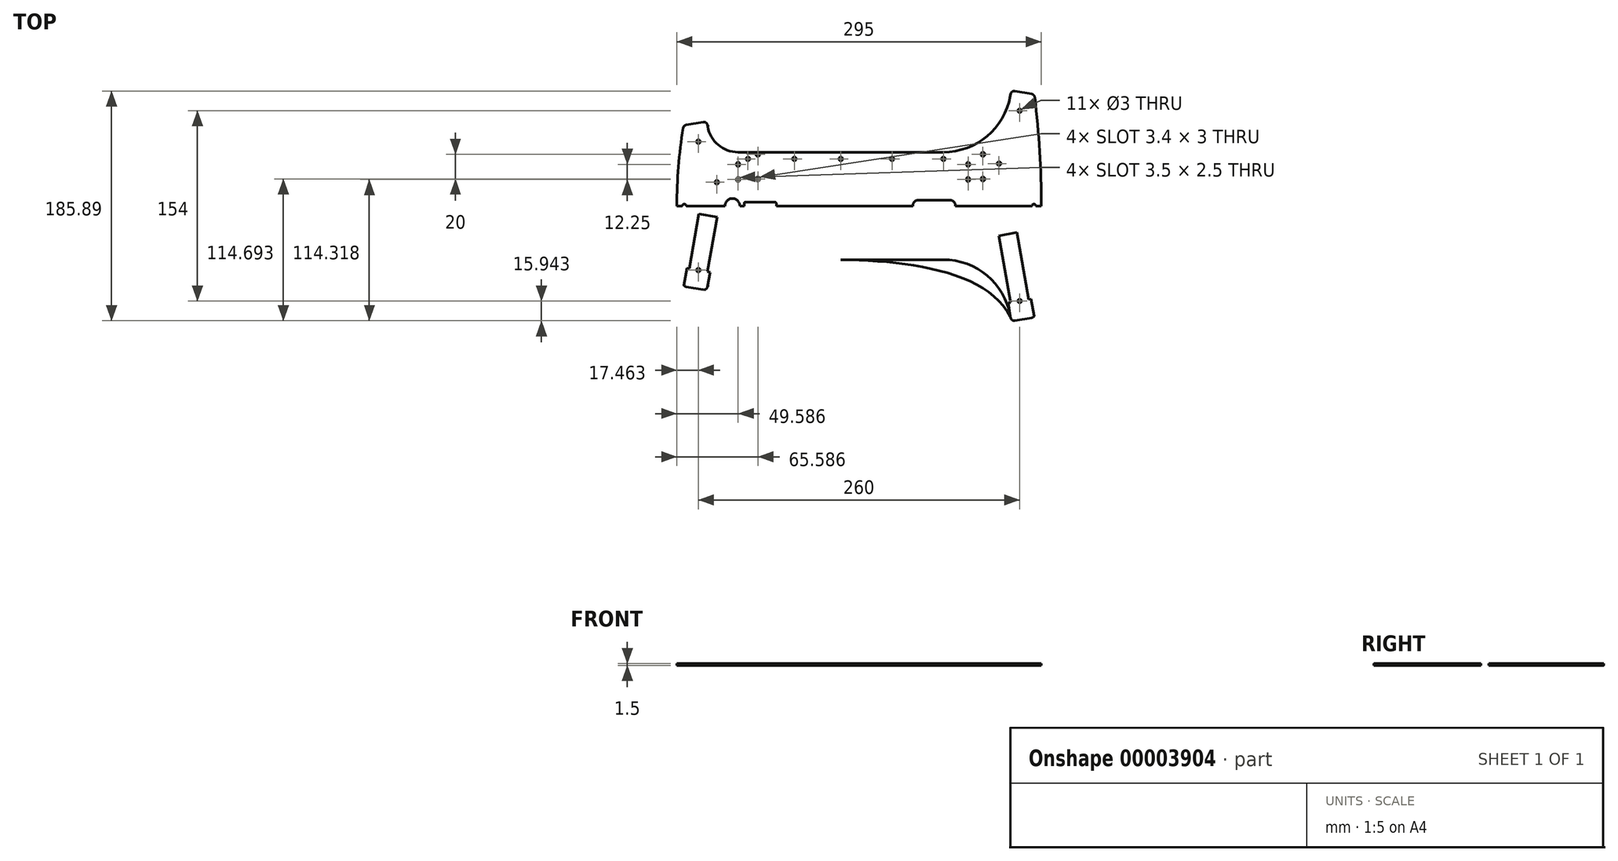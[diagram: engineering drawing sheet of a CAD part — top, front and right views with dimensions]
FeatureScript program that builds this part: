
annotation { "Feature Type Name" : "Feature", "Feature Type Description" : "" }
export const myFeature = defineFeature(function(context is Context, id is Id, definition is map)
    precondition{}
    {
        {
            var Q0;
            Q0=qCreatedBy(makeId("Top.planeOp"),FACE);
            var sketch = newSketch(context, id + "F0", { "sketchPlane" : qUnion([Q0])});
            skCircle(sketch, "E0", {"center": v(-144.57, -75.39) * mm, "radius": 1.5 * mm});
            skCircle(sketch, "E1", {"center": v(115.43, -100.39) * mm, "radius": 1.5 * mm});
            skLineSegment(sketch, "E2", {"start": v(132.97, -23.39) * mm, "end": v(-100.94, -23.39) * mm});
            skLineSegment(sketch, "E3", {"start": v(-154.44, -88.88) * mm, "end": v(-140.77, -91.29) * mm});
            skLineSegment(sketch, "E4", {"start": v(-137.3, -88.85) * mm, "end": v(-135.21, -77.04) * mm});
            skLineSegment(sketch, "E5", {"start": v(-135.21, -77.04) * mm, "end": v(-153.92, -73.74) * mm});
            skLineSegment(sketch, "E6", {"start": v(-153.92, -73.74) * mm, "end": v(-156.53, -88.5) * mm});
            skLineSegment(sketch, "E7", {"start": v(-137.06, -87.55) * mm, "end": v(-135.21, -77.04) * mm});
            skLineSegment(sketch, "E8", {"start": v(-112.44, -66.89) * mm, "end": v(53.73, -66.89) * mm});
            skLineSegment(sketch, "E9", {"start": v(-144.57, -75.39) * mm, "end": v(-174.96, -247.73) * mm});
            skLineSegment(sketch, "E10", {"start": v(106.08, -102.04) * mm, "end": v(124.79, -98.74) * mm});
            skLineSegment(sketch, "E11", {"start": v(124.79, -98.74) * mm, "end": v(127.4, -113.5) * mm});
            skLineSegment(sketch, "E12", {"start": v(125.2, -113.9) * mm, "end": v(111.64, -116.29) * mm});
            skLineSegment(sketch, "E13", {"start": v(108.16, -113.85) * mm, "end": v(106.08, -102.04) * mm});
            skLineSegment(sketch, "E14", {"start": v(115.43, -100.39) * mm, "end": v(141.48, -248.1) * mm});
            skLineSegment(sketch, "E15", {"start": v(107.9, -112.34) * mm, "end": v(106.08, -102.04) * mm});
            skPoint(sketch, "E16", {"position": v(122.82, -99.08) * mm});
            skPoint(sketch, "E17", {"position": v(108.05, -101.69) * mm});
            skLineSegment(sketch, "E18", {"start": v(108.05, -101.69) * mm, "end": v(98.5, -47.52) * mm});
            skLineSegment(sketch, "E19", {"start": v(98.5, -47.52) * mm, "end": v(113.27, -44.92) * mm});
            skLineSegment(sketch, "E20", {"start": v(113.27, -44.92) * mm, "end": v(122.82, -99.08) * mm});
            skPoint(sketch, "E21", {"position": v(-137.18, -76.69) * mm});
            skPoint(sketch, "E22", {"position": v(-151.95, -74.08) * mm});
            skLineSegment(sketch, "E23", {"start": v(-151.95, -74.08) * mm, "end": v(-144.14, -29.77) * mm});
            skLineSegment(sketch, "E24", {"start": v(-144.14, -29.77) * mm, "end": v(-129.37, -32.37) * mm});
            skLineSegment(sketch, "E25", {"start": v(-129.37, -32.37) * mm, "end": v(-137.18, -76.69) * mm});
            skCircle(sketch, "E26", {"center": v(-171.48, -228.03) * mm, "radius": 50 * mm});
            skCircle(sketch, "E27", {"center": v(138, -228.41) * mm, "radius": 50 * mm});
            skCircle(sketch, "E28", {"center": v(-144.57, 28.61) * mm, "radius": 1.5 * mm});
            skLineSegment(sketch, "E29", {"start": v(-144.14, -17) * mm, "end": v(-129.37, -14.4) * mm});
            skLineSegment(sketch, "E30", {"start": v(-129.37, -14.4) * mm, "end": v(-137.18, 29.92) * mm});
            skLineSegment(sketch, "E31", {"start": v(-137.18, 29.92) * mm, "end": v(-151.95, 27.31) * mm});
            skLineSegment(sketch, "E32", {"start": v(-151.95, 27.31) * mm, "end": v(-144.14, -17) * mm});
            skLineSegment(sketch, "E33", {"start": v(-137.18, 29.92) * mm, "end": v(-135.21, 30.26) * mm});
            skLineSegment(sketch, "E34", {"start": v(-151.95, 27.31) * mm, "end": v(-153.92, 26.96) * mm});
            skLineSegment(sketch, "E35", {"start": v(-135.21, 30.26) * mm, "end": v(-137.3, 42.08) * mm});
            skLineSegment(sketch, "E36", {"start": v(-140.77, 44.51) * mm, "end": v(-154.44, 42.1) * mm});
            skLineSegment(sketch, "E37", {"start": v(-156.53, 41.74) * mm, "end": v(-153.92, 26.96) * mm});
            skLineSegment(sketch, "E38", {"start": v(-112.44, 20.11) * mm, "end": v(53.73, 20.11) * mm});
            skLineSegment(sketch, "E39", {"start": v(-137.06, 40.77) * mm, "end": v(-135.21, 30.26) * mm});
            skCircle(sketch, "E40", {"center": v(115.43, 53.61) * mm, "radius": 1.5 * mm});
            skLineSegment(sketch, "E41", {"start": v(122.82, 52.31) * mm, "end": v(108.05, 54.92) * mm});
            skLineSegment(sketch, "E42", {"start": v(108.05, 54.92) * mm, "end": v(98.5, 0.75) * mm});
            skLineSegment(sketch, "E43", {"start": v(98.5, 0.75) * mm, "end": v(113.27, -1.85) * mm});
            skLineSegment(sketch, "E44", {"start": v(113.27, -1.85) * mm, "end": v(122.82, 52.31) * mm});
            skLineSegment(sketch, "E45", {"start": v(122.82, 52.31) * mm, "end": v(124.79, 51.96) * mm});
            skLineSegment(sketch, "E46", {"start": v(108.05, 54.92) * mm, "end": v(106.08, 55.26) * mm});
            skLineSegment(sketch, "E47", {"start": v(106.08, 55.26) * mm, "end": v(108.16, 67.08) * mm});
            skLineSegment(sketch, "E48", {"start": v(111.64, 69.51) * mm, "end": v(125.2, 67.12) * mm});
            skLineSegment(sketch, "E49", {"start": v(127.4, 66.74) * mm, "end": v(124.79, 51.96) * mm});
            skLineSegment(sketch, "E50", {"start": v(107.9, 65.56) * mm, "end": v(106.08, 55.26) * mm});
            skArc(sketch, "E51", {"start": v(-156.88, 39.64) * mm, "mid": v(-162.03, -23.39) * mm, "end": v(-156.88, -86.4) * mm});
            skArc(sketch, "E52", {"start": v(127.66, -111.3) * mm, "mid": v(132.97, -23.39) * mm, "end": v(127.66, 64.53) * mm});
            skPoint(sketch, "E53.visualSharp", {"position": v(-156.53, 41.74) * mm});
            skArc(sketch, "E53.filletArc", {"start": v(-154.44, 42.1) * mm, "mid": v(-156.05, 41.26) * mm, "end": v(-156.88, 39.64) * mm});
            skPoint(sketch, "E54.visualSharp", {"position": v(-137.82, 45.04) * mm});
            skArc(sketch, "E54.filletArc", {"start": v(-137.47, 42.7) * mm, "mid": v(-138.8, 44.19) * mm, "end": v(-140.77, 44.51) * mm});
            skPoint(sketch, "E55.visualSharp", {"position": v(-133.42, 20.11) * mm});
            skArc(sketch, "E55.filletArc", {"start": v(-137.06, 40.77) * mm, "mid": v(-128.51, 25.96) * mm, "end": v(-112.44, 20.11) * mm});
            skPoint(sketch, "E56.visualSharp", {"position": v(99.88, 20.11) * mm});
            skArc(sketch, "E56.filletArc", {"start": v(53.73, 20.11) * mm, "mid": v(89.08, 32.98) * mm, "end": v(107.9, 65.56) * mm});
            skPoint(sketch, "E57.visualSharp", {"position": v(108.68, 70.04) * mm});
            skArc(sketch, "E57.filletArc", {"start": v(111.64, 69.51) * mm, "mid": v(109.56, 69.13) * mm, "end": v(108.26, 67.47) * mm});
            skPoint(sketch, "E58.visualSharp", {"position": v(127.4, 66.74) * mm});
            skArc(sketch, "E58.filletArc", {"start": v(127.66, 64.53) * mm, "mid": v(126.86, 66.23) * mm, "end": v(125.2, 67.12) * mm});
            skPoint(sketch, "E59.visualSharp", {"position": v(127.4, -113.5) * mm});
            skArc(sketch, "E59.filletArc", {"start": v(125.2, -113.9) * mm, "mid": v(126.86, -113) * mm, "end": v(127.66, -111.3) * mm});
            skPoint(sketch, "E60.visualSharp", {"position": v(108.68, -116.8) * mm});
            skArc(sketch, "E60.filletArc", {"start": v(108.26, -114.24) * mm, "mid": v(109.56, -115.9) * mm, "end": v(111.64, -116.29) * mm});
            skPoint(sketch, "E61.visualSharp", {"position": v(99.88, -66.89) * mm});
            skArc(sketch, "E61.filletArc", {"start": v(107.9, -112.34) * mm, "mid": v(89.08, -79.75) * mm, "end": v(53.73, -66.89) * mm});
            skPoint(sketch, "E62.visualSharp", {"position": v(-133.42, -66.89) * mm});
            skArc(sketch, "E62.filletArc", {"start": v(-112.44, -66.89) * mm, "mid": v(-128.51, -72.74) * mm, "end": v(-137.06, -87.55) * mm});
            skPoint(sketch, "E63.visualSharp", {"position": v(-137.82, -91.8) * mm});
            skArc(sketch, "E63.filletArc", {"start": v(-140.77, -91.29) * mm, "mid": v(-138.8, -90.96) * mm, "end": v(-137.47, -89.47) * mm});
            skPoint(sketch, "E64.visualSharp", {"position": v(-156.53, -88.5) * mm});
            skArc(sketch, "E64.filletArc", {"start": v(-156.88, -86.4) * mm, "mid": v(-156.05, -88.03) * mm, "end": v(-154.44, -88.88) * mm});
            skCircle(sketch, "E65", {"center": v(-112.44, -2.51) * mm, "radius": 1.25 * mm});
            skCircle(sketch, "E66", {"center": v(-112.44, 9.74) * mm, "radius": 1.25 * mm});
            skCircle(sketch, "E67", {"center": v(-112.44, -1.51) * mm, "radius": 1.25 * mm});
            skCircle(sketch, "E68", {"center": v(-112.44, 10.74) * mm, "radius": 1.25 * mm});
            skLineSegment(sketch, "E69", {"start": v(-113.7, 14.13) * mm, "end": v(-113.7, 7.78) * mm});
            skLineSegment(sketch, "E70", {"start": v(-111.2, 14.21) * mm, "end": v(-111.2, 7.92) * mm});
            skLineSegment(sketch, "E71", {"start": v(-113.7, 0.03) * mm, "end": v(-113.7, -3.9) * mm});
            skLineSegment(sketch, "E72", {"start": v(-111.2, -0.35) * mm, "end": v(-111.2, -4.3) * mm});
            skCircle(sketch, "E73.0.MirrorC", {"center": v(-112.44, -57.51) * mm, "radius": 1.25 * mm});
            skLineSegment(sketch, "E73.1.MirrorCS", {"start": v(-113.7, -46.8) * mm, "end": v(-113.7, -42.87) * mm});
            skCircle(sketch, "E73.3.MirrorC", {"center": v(-112.44, -45.26) * mm, "radius": 1.25 * mm});
            skCircle(sketch, "E73.4.MirrorC", {"center": v(-112.44, -44.26) * mm, "radius": 1.25 * mm});
            skLineSegment(sketch, "E73.5.MirrorCS", {"start": v(-113.7, -60.9) * mm, "end": v(-113.7, -54.56) * mm});
            skLineSegment(sketch, "E73.10.MirrorCS", {"start": v(-111.2, -60.98) * mm, "end": v(-111.2, -54.7) * mm});
            skCircle(sketch, "E73.14.MirrorC", {"center": v(-112.44, -56.51) * mm, "radius": 1.25 * mm});
            skLineSegment(sketch, "E73.15.MirrorCS", {"start": v(-111.2, -46.43) * mm, "end": v(-111.2, -42.48) * mm});
            skPoint(sketch, "E74", {"position": v(-29.36, 20.11) * mm});
            skCircle(sketch, "E75", {"center": v(73.73, -2.51) * mm, "radius": 1.25 * mm});
            skCircle(sketch, "E76", {"center": v(73.73, 9.74) * mm, "radius": 1.25 * mm});
            skCircle(sketch, "E77", {"center": v(73.73, 10.74) * mm, "radius": 1.25 * mm});
            skCircle(sketch, "E78", {"center": v(73.73, -1.51) * mm, "radius": 1.25 * mm});
            skCircle(sketch, "E79", {"center": v(85.73, 18.56) * mm, "radius": 1.5 * mm});
            skCircle(sketch, "E80", {"center": v(85.73, 18.16) * mm, "radius": 1.5 * mm});
            skLineSegment(sketch, "E81", {"start": v(87.23, 16.25) * mm, "end": v(87.23, 20.23) * mm});
            skLineSegment(sketch, "E82", {"start": v(84.23, 16.35) * mm, "end": v(84.23, 20.42) * mm});
            skCircle(sketch, "E83.10.MirrorC", {"center": v(73.73, -44.26) * mm, "radius": 1.25 * mm});
            skCircle(sketch, "E83.11.MirrorC", {"center": v(73.73, -45.26) * mm, "radius": 1.25 * mm});
            skCircle(sketch, "E84.0.MirrorC", {"center": v(73.73, -56.51) * mm, "radius": 1.25 * mm});
            skCircle(sketch, "E84.3.MirrorC", {"center": v(73.73, -57.51) * mm, "radius": 1.25 * mm});
            skLineSegment(sketch, "E85", {"start": v(72.48, 14.9) * mm, "end": v(72.48, 6.98) * mm});
            skLineSegment(sketch, "E86", {"start": v(74.98, 7.58) * mm, "end": v(74.98, 14.93) * mm});
            skLineSegment(sketch, "E87", {"start": v(74.98, 0.09) * mm, "end": v(74.98, -4.2) * mm});
            skLineSegment(sketch, "E88", {"start": v(72.48, 0.48) * mm, "end": v(72.48, -4.36) * mm});
            skLineSegment(sketch, "E89.0.MirrorCS", {"start": v(72.48, -61.68) * mm, "end": v(72.48, -53.75) * mm});
            skLineSegment(sketch, "E90.0.MirrorCS", {"start": v(74.98, -54.36) * mm, "end": v(74.98, -61.7) * mm});
            skLineSegment(sketch, "E91.0.MirrorCS", {"start": v(72.48, -47.25) * mm, "end": v(72.48, -42.4) * mm});
            skLineSegment(sketch, "E92.0.MirrorCS", {"start": v(74.98, -46.86) * mm, "end": v(74.98, -42.58) * mm});
            skCircle(sketch, "E93", {"center": v(-104.44, 14.61) * mm, "radius": 1.5 * mm});
            skCircle(sketch, "E94", {"center": v(-29.36, 14.61) * mm, "radius": 1.5 * mm});
            skCircle(sketch, "E95", {"center": v(53.73, 14.61) * mm, "radius": 1.5 * mm});
            skCircle(sketch, "E96.0.MirrorC", {"center": v(-104.44, -61.39) * mm, "radius": 1.5 * mm});
            skCircle(sketch, "E97.0.MirrorC", {"center": v(-29.36, -61.39) * mm, "radius": 1.5 * mm});
            skCircle(sketch, "E98.0.MirrorC", {"center": v(53.73, -61.39) * mm, "radius": 1.5 * mm});
            skCircle(sketch, "E99", {"center": v(-156.03, -23.39) * mm, "radius": 1.5 * mm});
            skPoint(sketch, "E100", {"position": v(-131.1, -4.55) * mm});
            skCircle(sketch, "E101", {"center": v(-129.63, -4.3) * mm, "radius": 1.5 * mm});
            skCircle(sketch, "E102.0.MirrorC", {"center": v(-129.63, -42.48) * mm, "radius": 1.5 * mm});
            skPoint(sketch, "E103", {"position": v(100.23, 10.6) * mm});
            skCircle(sketch, "E104", {"center": v(98.76, 10.86) * mm, "radius": 1.5 * mm});
            skCircle(sketch, "E105.0.MirrorC", {"center": v(98.76, -57.63) * mm, "radius": 1.5 * mm});
            skPoint(sketch, "E106.0.MirrorP", {"position": v(100.23, -57.37) * mm});
            skCircle(sketch, "E107", {"center": v(-117.03, -23.39) * mm, "radius": 6 * mm});
            skLineSegment(sketch, "E108", {"start": v(-133.11, -23.39) * mm, "end": v(-162.03, -23.39) * mm});
            skLineSegment(sketch, "E109", {"start": v(-100.94, -23.39) * mm, "end": v(-133.11, -23.39) * mm});
            skFitSpline(sketch, "E110", {"points": [v(-137.3, 42.08) * mm, v(-29.36, 20.11) * mm, v(108.16, 67.08) * mm], "startDerivative": vector(83.4, -109.37) * mm, "endDerivative": vector(98.31, 207.46) * mm});
            skPoint(sketch, "E111", {"position": v(-29.36, -66.89) * mm});
            skArc(sketch, "E112.filletArc", {"start": v(-137.47, 42.7) * mm, "mid": v(-137.04, 41.84) * mm, "end": v(-136.47, 41.06) * mm});
            skArc(sketch, "E113.filletArc", {"start": v(107.8, 66.33) * mm, "mid": v(108.05, 66.89) * mm, "end": v(108.26, 67.47) * mm});
            skFitSpline(sketch, "E114", {"points": [v(-137.3, -88.85) * mm, v(-29.36, -66.89) * mm, v(108.16, -113.85) * mm], "startDerivative": vector(83.4, 109.37) * mm, "endDerivative": vector(98.31, -207.46) * mm});
            skArc(sketch, "E115.filletArc", {"start": v(-136.47, -87.84) * mm, "mid": v(-137.04, -88.62) * mm, "end": v(-137.47, -89.47) * mm});
            skArc(sketch, "E116.filletArc", {"start": v(108.26, -114.24) * mm, "mid": v(108.05, -113.66) * mm, "end": v(107.8, -113.1) * mm});
            skLineSegment(sketch, "E117", {"start": v(-29.36, 14.61) * mm, "end": v(53.73, 14.61) * mm});
            skCircle(sketch, "E118", {"center": v(12.19, 14.61) * mm, "radius": 1.5 * mm});
            skLineSegment(sketch, "E119", {"start": v(-104.44, 14.61) * mm, "end": v(-29.36, 14.61) * mm});
            skCircle(sketch, "E120", {"center": v(-66.9, 14.61) * mm, "radius": 1.5 * mm});
            skCircle(sketch, "E121.0.MirrorC", {"center": v(-66.9, -61.39) * mm, "radius": 1.5 * mm});
            skCircle(sketch, "E122.0.MirrorC", {"center": v(12.19, -61.39) * mm, "radius": 1.5 * mm});
            skPoint(sketch, "E123", {"position": v(73.73, 4.11) * mm});
            skCircle(sketch, "E124", {"center": v(-96.44, 18.56) * mm, "radius": 1.5 * mm});
            skCircle(sketch, "E125", {"center": v(-96.44, -1.44) * mm, "radius": 1.5 * mm});
            skCircle(sketch, "E126", {"center": v(-96.44, 18.16) * mm, "radius": 1.5 * mm});
            skCircle(sketch, "E127", {"center": v(-96.44, -1.84) * mm, "radius": 1.5 * mm});
            skLineSegment(sketch, "E128", {"start": v(-97.94, 19.82) * mm, "end": v(-97.94, 16.38) * mm});
            skLineSegment(sketch, "E129", {"start": v(-94.94, 19.9) * mm, "end": v(-94.94, 16.28) * mm});
            skLineSegment(sketch, "E130", {"start": v(-97.94, 0.25) * mm, "end": v(-97.94, -3.67) * mm});
            skLineSegment(sketch, "E131", {"start": v(-94.94, 0.3) * mm, "end": v(-94.94, -3.5) * mm});
            skLineSegment(sketch, "E132.0.MirrorCS", {"start": v(-94.94, -47.07) * mm, "end": v(-94.94, -43.28) * mm});
            skLineSegment(sketch, "E132.1.MirrorCS", {"start": v(-97.94, -47.02) * mm, "end": v(-97.94, -43.1) * mm});
            skCircle(sketch, "E132.2.MirrorC", {"center": v(-96.44, -45.34) * mm, "radius": 1.5 * mm});
            skCircle(sketch, "E132.3.MirrorC", {"center": v(-96.44, -44.94) * mm, "radius": 1.5 * mm});
            skCircle(sketch, "E133.0.MirrorC", {"center": v(-96.44, -65.34) * mm, "radius": 1.5 * mm});
            skCircle(sketch, "E133.1.MirrorC", {"center": v(-96.44, -64.94) * mm, "radius": 1.5 * mm});
            skLineSegment(sketch, "E133.2.MirrorCS", {"start": v(-97.94, -66.6) * mm, "end": v(-97.94, -63.15) * mm});
            skLineSegment(sketch, "E133.3.MirrorCS", {"start": v(-94.94, -66.68) * mm, "end": v(-94.94, -63.06) * mm});
            skCircle(sketch, "E134", {"center": v(85.73, -1.44) * mm, "radius": 1.5 * mm});
            skCircle(sketch, "E135", {"center": v(85.73, -1.84) * mm, "radius": 1.5 * mm});
            skLineSegment(sketch, "E136", {"start": v(84.23, 0.33) * mm, "end": v(84.23, -3.55) * mm});
            skLineSegment(sketch, "E137", {"start": v(87.23, 0.52) * mm, "end": v(87.23, -3.48) * mm});
            skLineSegment(sketch, "E138.0.MirrorCS", {"start": v(87.23, -63.02) * mm, "end": v(87.23, -67) * mm});
            skLineSegment(sketch, "E138.1.MirrorCS", {"start": v(84.23, -63.12) * mm, "end": v(84.23, -67.2) * mm});
            skCircle(sketch, "E138.2.MirrorC", {"center": v(85.73, -65.34) * mm, "radius": 1.5 * mm});
            skCircle(sketch, "E138.3.MirrorC", {"center": v(85.73, -64.94) * mm, "radius": 1.5 * mm});
            skCircle(sketch, "E139.0.MirrorC", {"center": v(85.73, -45.34) * mm, "radius": 1.5 * mm});
            skLineSegment(sketch, "E139.1.MirrorCS", {"start": v(87.23, -47.29) * mm, "end": v(87.23, -43.29) * mm});
            skLineSegment(sketch, "E139.2.MirrorCS", {"start": v(84.23, -47.1) * mm, "end": v(84.23, -43.23) * mm});
            skCircle(sketch, "E139.3.MirrorC", {"center": v(85.73, -44.94) * mm, "radius": 1.5 * mm});
            skLineSegment(sketch, "E140", {"start": v(-112.44, 9.74) * mm, "end": v(-112.44, -1.51) * mm});
            skPoint(sketch, "E141", {"position": v(-112.44, 4.11) * mm});
            skPoint(sketch, "E142", {"position": v(-94.53, -23.39) * mm});
            skLineSegment(sketch, "E143.bottom", {"start": v(-106.53, -20.39) * mm, "end": v(-82.53, -20.39) * mm});
            skLineSegment(sketch, "E143.top", {"start": v(-106.53, -26.39) * mm, "end": v(-82.53, -26.39) * mm});
            skLineSegment(sketch, "E143.left", {"start": v(-107.53, -21.39) * mm, "end": v(-107.53, -25.39) * mm});
            skLineSegment(sketch, "E143.right", {"start": v(-81.53, -21.39) * mm, "end": v(-81.53, -25.39) * mm});
            skPoint(sketch, "E144.visualSharp", {"position": v(-107.53, -20.39) * mm});
            skArc(sketch, "E144.filletArc", {"start": v(-106.53, -20.39) * mm, "mid": v(-107.23, -20.68) * mm, "end": v(-107.53, -21.39) * mm});
            skPoint(sketch, "E145.visualSharp", {"position": v(-107.53, -26.39) * mm});
            skArc(sketch, "E145.filletArc", {"start": v(-107.53, -25.39) * mm, "mid": v(-107.23, -26.1) * mm, "end": v(-106.53, -26.39) * mm});
            skPoint(sketch, "E146.visualSharp", {"position": v(-81.53, -20.39) * mm});
            skArc(sketch, "E146.filletArc", {"start": v(-81.53, -21.39) * mm, "mid": v(-81.82, -20.68) * mm, "end": v(-82.53, -20.39) * mm});
            skPoint(sketch, "E147.visualSharp", {"position": v(-81.53, -26.39) * mm});
            skArc(sketch, "E147.filletArc", {"start": v(-82.53, -26.39) * mm, "mid": v(-81.82, -26.1) * mm, "end": v(-81.53, -25.39) * mm});
            skCircle(sketch, "E148", {"center": v(58.73, -23.39) * mm, "radius": 4.75 * mm});
            skCircle(sketch, "E149", {"center": v(33.73, -23.39) * mm, "radius": 4.75 * mm});
            skLineSegment(sketch, "E150", {"start": v(68.42, -18.64) * mm, "end": v(4.54, -18.64) * mm});
            skLineSegment(sketch, "E151", {"start": v(4.26, -28.14) * mm, "end": v(69.1, -28.14) * mm});
            skCircle(sketch, "E152", {"center": v(126.97, -23.39) * mm, "radius": 1.5 * mm});
            skSolve(sketch);
        }
        {
            var Q0;
            {var subQ5=sQuery(id+"F0.wireOp",EDGE,"E45");Q0=makeQuery(id+"F0.imprint","IMPRINT",FACE,{"disambiguationData":[TD([[makeQuery(id+"F0.imprint","IMPRINT",EDGE,{"derivedFrom":subQ5}),1.0]])]});}
            var Q1;
            {var subQ5=sQuery(id+"F0.wireOp",EDGE,"E6");Q1=makeQuery(id+"F0.imprint","IMPRINT",FACE,{"disambiguationData":[TD([[makeQuery(id+"F0.imprint","IMPRINT",EDGE,{"derivedFrom":subQ5}),1.0]])]});}
            var Q2;
            {var subQ8=sQuery(id+"F0.wireOp",EDGE,"E4");Q2=makeQuery(id+"F0.imprint","IMPRINT",FACE,{"disambiguationData":[TD([[makeQuery(id+"F0.imprint","IMPRINT",EDGE,{"derivedFrom":subQ8}),1.0]])]});}
            var Q3;
            {var subQ5=sQuery(id+"F0.wireOp",EDGE,"E13");Q3=makeQuery(id+"F0.imprint","IMPRINT",FACE,{"disambiguationData":[TD([[makeQuery(id+"F0.imprint","IMPRINT",EDGE,{"derivedFrom":subQ5}),-1.0]])]});}
            var Q4;
            {var subQ3=sQuery(id+"F0.wireOp",EDGE,"E11");Q4=makeQuery(id+"F0.imprint","IMPRINT",FACE,{"disambiguationData":[TD([[makeQuery(id+"F0.imprint","IMPRINT",EDGE,{"derivedFrom":subQ3}),-1.0]])]});}
            var Q5;
            {var subQ1=sQuery(id+"F0.wireOp",EDGE,"E23");Q5=makeQuery(id+"F0.imprint","IMPRINT",FACE,{"disambiguationData":[TD([[makeQuery(id+"F0.imprint","IMPRINT",EDGE,{"derivedFrom":subQ1}),-1.0]])]});}
            var Q6;
            {var subQ1=sQuery(id+"F0.wireOp",EDGE,"E18");Q6=makeQuery(id+"F0.imprint","IMPRINT",FACE,{"disambiguationData":[TD([[makeQuery(id+"F0.imprint","IMPRINT",EDGE,{"derivedFrom":subQ1}),-1.0]])]});}
            var Q7;
            {var subQ0=sQuery(id+"F0.wireOp",EDGE,"E42");Q7=makeQuery(id+"F0.imprint","IMPRINT",FACE,{"disambiguationData":[TD([[makeQuery(id+"F0.imprint","IMPRINT",EDGE,{"derivedFrom":subQ0}),1.0]])]});}
            var Q8;
            Q8=makeQuery(id+"F0.imprint","IMPRINT",FACE,{"disambiguationData":[TD([[makeQuery(id+"F0.imprint","IMPRINT",EDGE,{"derivedFrom":sQuery(id+"F0.wireOp",EDGE,"0409cc0b-147e-460b-8b65-a1790570d2e4")}),-1.0]])]});
            var Q9;
            Q9=makeQuery(id+"F0.imprint","IMPRINT",FACE,{"disambiguationData":[TD([[makeQuery(id+"F0.imprint","IMPRINT",EDGE,{"derivedFrom":sQuery(id+"F0.wireOp",EDGE,"595f4188-ce56-4ccc-9c5c-739e4f8723a3.0.MirrorC")}),-1.0]])]});
            var Q10;
            {var subQ184=sQuery(id+"F0.wireOp",EDGE,"E7");Q10=makeQuery(id+"F0.imprint","IMPRINT",FACE,{"disambiguationData":[TD([[makeQuery(id+"F0.imprint","IMPRINT",EDGE,{"derivedFrom":subQ184}),-1.0]])]});}
            var Q11;
            Q11=makeQuery(id+"F0.imprint","IMPRINT",FACE,{"disambiguationData":[TD([[makeQuery(id+"F0.imprint","IMPRINT",EDGE,{"derivedFrom":sQuery(id+"F0.wireOp",EDGE,"E13")}),1.0]])]});
            var Q12;
            {var subQ10=sQuery(id+"F0.wireOp",EDGE,"E33");Q12=makeQuery(id+"F0.imprint","IMPRINT",FACE,{"disambiguationData":[TD([[makeQuery(id+"F0.imprint","IMPRINT",EDGE,{"derivedFrom":subQ10}),1.0]])]});}
            var Q13;
            {var subQ8=sQuery(id+"F0.wireOp",EDGE,"E29");Q13=makeQuery(id+"F0.imprint","IMPRINT",FACE,{"disambiguationData":[TD([[makeQuery(id+"F0.imprint","IMPRINT",EDGE,{"derivedFrom":subQ8}),1.0]])]});}
            var Q14;
            {var subQ114=sQuery(id+"F0.wireOp",EDGE,"E29");Q14=makeQuery(id+"F0.imprint","IMPRINT",FACE,{"disambiguationData":[TD([[makeQuery(id+"F0.imprint","IMPRINT",EDGE,{"derivedFrom":subQ114}),-1.0]])]});}
            var Q15;
            {var subQ0=sQuery(id+"F0.wireOp",EDGE,"bacfffff-6067-4d1f-9cf2-934ef041a62e.10.MirrorC");var subQ2=makeQuery(id+"F0.imprint","INTERSECT",VERTEX,{"derivedFrom":[sQuery(id+"F0.wireOp",EDGE,"bacfffff-6067-4d1f-9cf2-934ef041a62e.1.MirrorCS"),subQ0]});Q15=makeQuery(id+"F0.imprint","IMPRINT",FACE,{"disambiguationData":[TD([[makeQuery(id+"F0.imprint","IMPRINT",EDGE,{"disambiguationData":[TD([[subQ2,-1.0]])],"derivedFrom":subQ0}),-1.0]])]});}
            var Q16;
            {var subQ3=sQuery(id+"F0.wireOp",EDGE,"bacfffff-6067-4d1f-9cf2-934ef041a62e.1.MirrorCS");var subQ5=sQuery(id+"F0.wireOp",EDGE,"bacfffff-6067-4d1f-9cf2-934ef041a62e.10.MirrorC");var subQ7=makeQuery(id+"F0.imprint","INTERSECT",VERTEX,{"derivedFrom":[subQ3,subQ5]});Q16=makeQuery(id+"F0.imprint","IMPRINT",FACE,{"disambiguationData":[TD([[makeQuery(id+"F0.imprint","IMPRINT",EDGE,{"disambiguationData":[TD([[subQ7,-1.0]])],"derivedFrom":subQ3}),1.0]])]});}
            var Q17;
            {var subQ0=sQuery(id+"F0.wireOp",EDGE,"bacfffff-6067-4d1f-9cf2-934ef041a62e.12.MirrorC");var subQ2=makeQuery(id+"F0.imprint","INTERSECT",VERTEX,{"derivedFrom":[sQuery(id+"F0.wireOp",EDGE,"bacfffff-6067-4d1f-9cf2-934ef041a62e.1.MirrorCS"),subQ0]});Q17=makeQuery(id+"F0.imprint","IMPRINT",FACE,{"disambiguationData":[TD([[makeQuery(id+"F0.imprint","IMPRINT",EDGE,{"disambiguationData":[TD([[subQ2,-1.0]])],"derivedFrom":subQ0}),-1.0]])]});}
            var Q18;
            {var subQ3=sQuery(id+"F0.wireOp",EDGE,"bacfffff-6067-4d1f-9cf2-934ef041a62e.3.MirrorC");var subQ5=sQuery(id+"F0.wireOp",EDGE,"bacfffff-6067-4d1f-9cf2-934ef041a62e.9.MirrorCS");var subQ7=makeQuery(id+"F0.imprint","INTERSECT",VERTEX,{"derivedFrom":[subQ3,subQ5]});Q18=makeQuery(id+"F0.imprint","IMPRINT",FACE,{"disambiguationData":[TD([[makeQuery(id+"F0.imprint","IMPRINT",EDGE,{"disambiguationData":[TD([[subQ7,-1.0]])],"derivedFrom":subQ3}),1.0]])]});}
            var Q19;
            {var subQ0=sQuery(id+"F0.wireOp",EDGE,"bacfffff-6067-4d1f-9cf2-934ef041a62e.7.MirrorC");var subQ2=makeQuery(id+"F0.imprint","INTERSECT",VERTEX,{"derivedFrom":[subQ0,sQuery(id+"F0.wireOp",EDGE,"bacfffff-6067-4d1f-9cf2-934ef041a62e.9.MirrorCS")]});Q19=makeQuery(id+"F0.imprint","IMPRINT",FACE,{"disambiguationData":[TD([[makeQuery(id+"F0.imprint","IMPRINT",EDGE,{"disambiguationData":[TD([[subQ2,-1.0]])],"derivedFrom":subQ0}),-1.0]])]});}
            var Q20;
            {var subQ0=sQuery(id+"F0.wireOp",EDGE,"bacfffff-6067-4d1f-9cf2-934ef041a62e.3.MirrorC");var subQ2=makeQuery(id+"F0.imprint","INTERSECT",VERTEX,{"derivedFrom":[subQ0,sQuery(id+"F0.wireOp",EDGE,"bacfffff-6067-4d1f-9cf2-934ef041a62e.9.MirrorCS")]});Q20=makeQuery(id+"F0.imprint","IMPRINT",FACE,{"disambiguationData":[TD([[makeQuery(id+"F0.imprint","IMPRINT",EDGE,{"disambiguationData":[TD([[subQ2,-1.0]])],"derivedFrom":subQ0}),-1.0]])]});}
            var Q21;
            {var subQ1=sQuery(id+"F0.wireOp",EDGE,"bacfffff-6067-4d1f-9cf2-934ef041a62e.5.MirrorC");var subQ5=sQuery(id+"F0.wireOp",EDGE,"E2");var subQ6=makeQuery(id+"F0.imprint","INTERSECT",VERTEX,{"disambiguationData":[OD(1.0)],"derivedFrom":[subQ5,subQ1]});Q21=makeQuery(id+"F0.imprint","IMPRINT",FACE,{"disambiguationData":[TD([[makeQuery(id+"F0.imprint","IMPRINT",EDGE,{"disambiguationData":[TD([[subQ6,-1.0]])],"derivedFrom":subQ5}),-1.0]])]});}
            var Q22;
            {var subQ1=sQuery(id+"F0.wireOp",EDGE,"bacfffff-6067-4d1f-9cf2-934ef041a62e.5.MirrorC");var subQ5=sQuery(id+"F0.wireOp",EDGE,"E2");var subQ6=makeQuery(id+"F0.imprint","INTERSECT",VERTEX,{"disambiguationData":[OD(1.0)],"derivedFrom":[subQ5,subQ1]});Q22=makeQuery(id+"F0.imprint","IMPRINT",FACE,{"disambiguationData":[TD([[makeQuery(id+"F0.imprint","IMPRINT",EDGE,{"disambiguationData":[TD([[subQ6,-1.0]])],"derivedFrom":subQ5}),1.0]])]});}
            var Q23;
            {var subQ3=sQuery(id+"F0.wireOp",EDGE,"1879b1f9-001d-4b70-bd42-4f96f4cbef81");var subQ5=sQuery(id+"F0.wireOp",EDGE,"44c3974b-f504-42e0-985f-4f0ac57ea7bc");var subQ7=makeQuery(id+"F0.imprint","INTERSECT",VERTEX,{"derivedFrom":[subQ3,subQ5]});Q23=makeQuery(id+"F0.imprint","IMPRINT",FACE,{"disambiguationData":[TD([[makeQuery(id+"F0.imprint","IMPRINT",EDGE,{"disambiguationData":[TD([[subQ7,-1.0]])],"derivedFrom":subQ3}),-1.0]])]});}
            var Q24;
            {var subQ3=sQuery(id+"F0.wireOp",EDGE,"440c2c23-d06a-4bbe-ada5-72bbf3f33836");var subQ5=sQuery(id+"F0.wireOp",EDGE,"504fca63-94b3-46d7-8850-182794d53c22");var subQ7=makeQuery(id+"F0.imprint","INTERSECT",VERTEX,{"derivedFrom":[subQ3,subQ5]});Q24=makeQuery(id+"F0.imprint","IMPRINT",FACE,{"disambiguationData":[TD([[makeQuery(id+"F0.imprint","IMPRINT",EDGE,{"disambiguationData":[TD([[subQ7,-1.0]])],"derivedFrom":subQ3}),-1.0]])]});}
            var Q25;
            {var subQ0=sQuery(id+"F0.wireOp",EDGE,"3ed2204c-2933-4181-93a2-7fd6f123b82e");var subQ2=makeQuery(id+"F0.imprint","INTERSECT",VERTEX,{"derivedFrom":[subQ0,sQuery(id+"F0.wireOp",EDGE,"44c3974b-f504-42e0-985f-4f0ac57ea7bc")]});Q25=makeQuery(id+"F0.imprint","IMPRINT",FACE,{"disambiguationData":[TD([[makeQuery(id+"F0.imprint","IMPRINT",EDGE,{"disambiguationData":[TD([[subQ2,-1.0]])],"derivedFrom":subQ0}),1.0]])]});}
            var Q26;
            {var subQ0=sQuery(id+"F0.wireOp",EDGE,"fd0d401a-6b05-4e9f-b845-53676f80a28f");var subQ2=makeQuery(id+"F0.imprint","INTERSECT",VERTEX,{"derivedFrom":[subQ0,sQuery(id+"F0.wireOp",EDGE,"504fca63-94b3-46d7-8850-182794d53c22")]});Q26=makeQuery(id+"F0.imprint","IMPRINT",FACE,{"disambiguationData":[TD([[makeQuery(id+"F0.imprint","IMPRINT",EDGE,{"disambiguationData":[TD([[subQ2,-1.0]])],"derivedFrom":subQ0}),1.0]])]});}
            var Q27;
            {var subQ0=sQuery(id+"F0.wireOp",EDGE,"440c2c23-d06a-4bbe-ada5-72bbf3f33836");var subQ2=makeQuery(id+"F0.imprint","INTERSECT",VERTEX,{"derivedFrom":[subQ0,sQuery(id+"F0.wireOp",EDGE,"504fca63-94b3-46d7-8850-182794d53c22")]});Q27=makeQuery(id+"F0.imprint","IMPRINT",FACE,{"disambiguationData":[TD([[makeQuery(id+"F0.imprint","IMPRINT",EDGE,{"disambiguationData":[TD([[subQ2,-1.0]])],"derivedFrom":subQ0}),1.0]])]});}
            var Q28;
            {var subQ0=sQuery(id+"F0.wireOp",EDGE,"1879b1f9-001d-4b70-bd42-4f96f4cbef81");var subQ2=makeQuery(id+"F0.imprint","INTERSECT",VERTEX,{"derivedFrom":[subQ0,sQuery(id+"F0.wireOp",EDGE,"44c3974b-f504-42e0-985f-4f0ac57ea7bc")]});Q28=makeQuery(id+"F0.imprint","IMPRINT",FACE,{"disambiguationData":[TD([[makeQuery(id+"F0.imprint","IMPRINT",EDGE,{"disambiguationData":[TD([[subQ2,-1.0]])],"derivedFrom":subQ0}),1.0]])]});}
            extrude(context, id + "F1", {"entities" : qUnion([Q0, Q1, Q2, Q3, Q4, Q5, Q6, Q7, Q8, Q9, Q10, Q11, Q12, Q13, Q14, Q15, Q16, Q17, Q18, Q19, Q20, Q21, Q22, Q23, Q24, Q25, Q26, Q27, Q28]), "depth" : 1.5 * mm});
        }
    });
